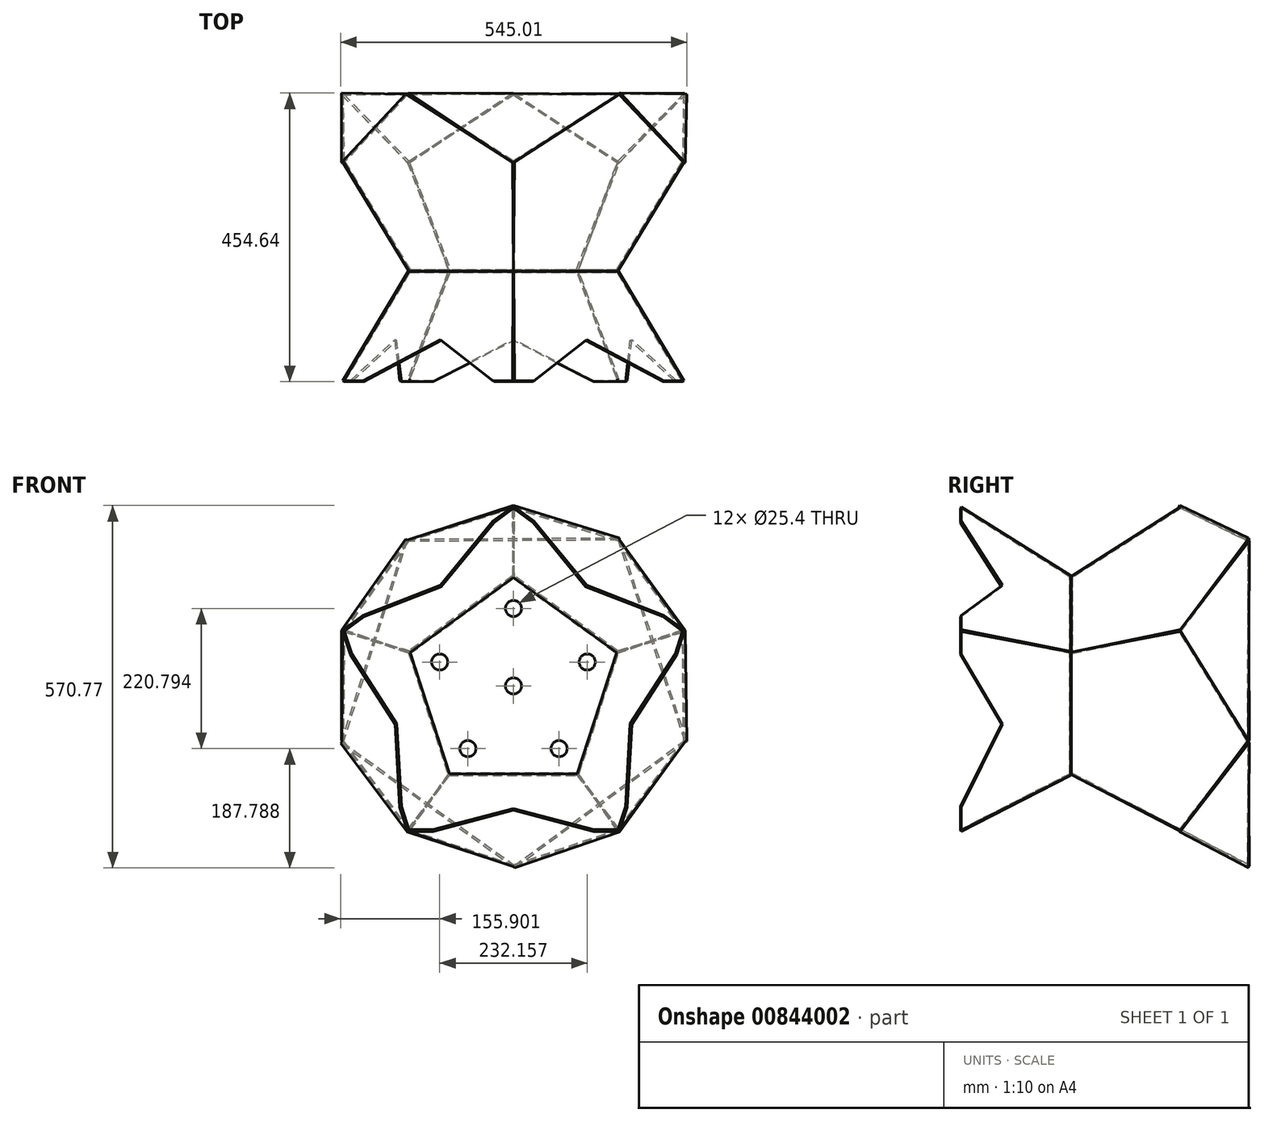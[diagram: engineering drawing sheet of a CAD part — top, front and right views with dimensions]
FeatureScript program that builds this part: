
annotation { "Feature Type Name" : "Feature", "Feature Type Description" : "" }
export const myFeature = defineFeature(function(context is Context, id is Id, definition is map)
    precondition{}
    {
        {
            var Q0;
            Q0=qCreatedBy(makeId("Front.planeOp"),FACE);
            var sketch = newSketch(context, id + "F0", { "sketchPlane" : qUnion([Q0])});
            skCircle(sketch, "E0.cCircle", {"center": v(0, 0) * mm, "radius": 139.84 * mm, "construction": true});
            skLineSegment(sketch, "E0.0", {"start": v(0, 172.85) * mm, "end": v(164.4, 53.41) * mm});
            skLineSegment(sketch, "E0.1", {"start": v(164.4, 53.41) * mm, "end": v(101.6, -139.84) * mm});
            skLineSegment(sketch, "E0.2", {"start": v(101.6, -139.84) * mm, "end": v(-101.6, -139.84) * mm});
            skLineSegment(sketch, "E0.3", {"start": v(-101.6, -139.84) * mm, "end": v(-164.4, 53.41) * mm});
            skLineSegment(sketch, "E0.4", {"start": v(-164.4, 53.41) * mm, "end": v(0, 172.85) * mm});
            skPoint(sketch, "E0.0.midPoint", {"position": v(82.2, 113.13) * mm});
            skCircle(sketch, "E1", {"center": v(0, 0) * mm, "radius": 122.05 * mm, "construction": true});
            skCircle(sketch, "E2", {"center": v(0, 122.05) * mm, "radius": 12.7 * mm});
            skCircle(sketch, "E3.1.0", {"center": v(-116.08, 37.72) * mm, "radius": 12.7 * mm});
            skCircle(sketch, "E3.2.0", {"center": v(-71.74, -98.74) * mm, "radius": 12.7 * mm});
            skCircle(sketch, "E4.1.3.0", {"center": v(71.74, -98.74) * mm, "radius": 12.7 * mm});
            skCircle(sketch, "E4.1.4.0", {"center": v(116.08, 37.72) * mm, "radius": 12.7 * mm});
            skCircle(sketch, "E5", {"center": v(0, 0) * mm, "radius": 12.7 * mm});
            skSolve(sketch);
        }
        {
            var Q0;
            Q0=makeQuery(id+"F0.imprint","IMPRINT",FACE,{"disambiguationData":[TD([[makeQuery(id+"F0.imprint","IMPRINT",EDGE,{"derivedFrom":sQuery(id+"F0.wireOp",EDGE,"E0.0")}),-1.0]])]});
            extrude(context, id + "F1", {"entities" : qUnion([Q0]), "endBound" : BoundingType.SYMMETRIC, "depth" : 3.17 * mm, "offsetDistance" : 25.4 * mm});
        }
        {
            var Q0;
            Q0=makeQuery(id+"F1.opExtrude","CAP_EDGE",EDGE,{"disambiguationData":[OSD([sQuery(id+"F0.wireOp",EDGE,"E0.1")])],"isStart":true});
            cPlane(context, id + "F2", {"entities" : qUnion([Q0]), "cplaneType" : CPlaneType.LINE_ANGLE, "offset" : 25.4 * mm, "angle" : 27.09 * degree, "oppositeDirection" : true, "width" : 152.4 * mm, "height" : 152.4 * mm});
        }
        {
            var Q0;
            Q0=qCreatedBy(id+"F2.planeOp",FACE);
            var sketch = newSketch(context, id + "F3", { "sketchPlane" : qUnion([Q0])});
            skArc(sketch, "E6.cCircle", {"start": v(258.35, 129.24) * mm, "mid": v(65.1, 0) * mm, "end": v(258.35, -129.24) * mm, "construction": true});
            skLineSegment(sketch, "E6.0", {"start": v(65.1, -101.6) * mm, "end": v(65.1, 101.6) * mm});
            skLineSegment(sketch, "E6.1", {"start": v(65.1, 101.6) * mm, "end": v(258.35, 164.4) * mm});
            skLineSegment(sketch, "E6.4", {"start": v(258.35, -164.4) * mm, "end": v(65.1, -101.6) * mm});
            skPoint(sketch, "E6.0.midPoint", {"position": v(65.1, 0) * mm});
            skLineSegment(sketch, "E7", {"start": v(258.35, 164.4) * mm, "end": v(258.35, 126.3) * mm});
            skLineSegment(sketch, "E8", {"start": v(258.35, 126.3) * mm, "end": v(185.44, 0) * mm});
            skLineSegment(sketch, "E9", {"start": v(258.35, -126.3) * mm, "end": v(185.44, 0) * mm});
            skLineSegment(sketch, "E10.trimOffspring", {"start": v(258.35, -126.3) * mm, "end": v(258.35, -164.4) * mm});
            skSolve(sketch);
        }
        {
            var Q0;
            Q0 = qSketchRegion(id + "F3", true);
            extrude(context, id + "F4", {"entities" : qUnion([Q0]), "depth" : 3.17 * mm, "offsetDistance" : 25.4 * mm});
        }
        {
            var Q0;
            Q0=makeQuery(id+"F4.opExtrude","SWEPT_BODY",BODY,{"disambiguationData":[OSD([sQuery(id+"F3.wireOp",EDGE,"E6.0"),sQuery(id+"F3.wireOp",EDGE,"E6.1"),sQuery(id+"F3.wireOp",EDGE,"E6.4"),sQuery(id+"F3.wireOp",EDGE,"E7"),sQuery(id+"F3.wireOp",EDGE,"E8"),sQuery(id+"F3.wireOp",EDGE,"E9"),sQuery(id+"F3.wireOp",EDGE,"E10.trimOffspring")])]});
            var Q1;
            Q1=sQuery(id+"F0.wireOp",EDGE,"E0.cCircle");
            circularPattern(context, id + "F5", {"entities" : qUnion([Q0]), "axis" : qUnion([Q1]), "angle" : 360 * degree, "instanceCount" : 5, "equalSpace" : true});
        }
        {
            var Q0;
            Q0=sQuery(id+"F0.wireOp",EDGE,"E0.0");
            cPlane(context, id + "F6", {"entities" : qUnion([Q0]), "cplaneType" : CPlaneType.LINE_ANGLE, "offset" : 25.4 * mm, "angle" : 62.5 * degree, "oppositeDirection" : true, "width" : 152.4 * mm, "height" : 152.4 * mm});
        }
        {
            var Q0;
            Q0=qCreatedBy(id+"F6.planeOp",FACE);
            var sketch = newSketch(context, id + "F7", { "sketchPlane" : qUnion([Q0])});
            skCircle(sketch, "E11.cCircle", {"center": v(65.01, -193.8) * mm, "radius": 139.84 * mm, "construction": true});
            skLineSegment(sketch, "E11.0", {"start": v(120, -357.67) * mm, "end": v(-73.85, -296.72) * mm});
            skLineSegment(sketch, "E11.1", {"start": v(-73.85, -296.72) * mm, "end": v(-75.79, -93.53) * mm});
            skLineSegment(sketch, "E11.2", {"start": v(-75.79, -93.53) * mm, "end": v(116.86, -28.9) * mm});
            skLineSegment(sketch, "E11.3", {"start": v(116.86, -28.9) * mm, "end": v(237.86, -192.15) * mm});
            skLineSegment(sketch, "E11.4", {"start": v(237.86, -192.15) * mm, "end": v(120, -357.67) * mm});
            skPoint(sketch, "E11.0.midPoint", {"position": v(23.07, -327.2) * mm});
            skSolve(sketch);
        }
        {
            var Q0;
            Q0 = qSketchRegion(id + "F7", true);
            extrude(context, id + "F8", {"entities" : qUnion([Q0]), "depth" : 3.17 * mm, "offsetDistance" : 25.4 * mm});
        }
        {
            var Q0;
            Q0=makeQuery(id+"F8.opExtrude","SWEPT_BODY",BODY,{"disambiguationData":[OSD([sQuery(id+"F7.wireOp",EDGE,"E11.0"),sQuery(id+"F7.wireOp",EDGE,"E11.1"),sQuery(id+"F7.wireOp",EDGE,"E11.2"),sQuery(id+"F7.wireOp",EDGE,"E11.3"),sQuery(id+"F7.wireOp",EDGE,"E11.4")])]});
            var Q1;
            Q1=sQuery(id+"F0.wireOp",EDGE,"E0.cCircle");
            circularPattern(context, id + "F9", {"entities" : qUnion([Q0]), "axis" : qUnion([Q1]), "angle" : 360 * degree, "instanceCount" : 5, "equalSpace" : true});
        }
        {
            var Q0;
            Q0=makeQuery(id+"F9.opPattern","COPY",VERTEX,{"derivedFrom":makeQuery(id+"F8.opExtrude","CAP_VERTEX",VERTEX,{"disambiguationData":[OSD([sQuery(id+"F7.wireOp",EDGE,"E11.0"),sQuery(id+"F7.wireOp",EDGE,"E11.4")])],"isStart":false}),"instanceName":"2"});
            var Q1;
            Q1=makeQuery(id+"F9.opPattern","COPY",VERTEX,{"derivedFrom":makeQuery(id+"F8.opExtrude","CAP_VERTEX",VERTEX,{"disambiguationData":[OSD([sQuery(id+"F7.wireOp",EDGE,"E11.0"),sQuery(id+"F7.wireOp",EDGE,"E11.4")])],"isStart":true}),"instanceName":"1"});
            var Q2;
            Q2=makeQuery(id+"F9.opPattern","COPY",VERTEX,{"derivedFrom":makeQuery(id+"F8.opExtrude","CAP_VERTEX",VERTEX,{"disambiguationData":[OSD([sQuery(id+"F7.wireOp",EDGE,"E11.0"),sQuery(id+"F7.wireOp",EDGE,"E11.1")])],"isStart":false}),"instanceName":"1"});
            cPlane(context, id + "F10", {"entities" : qUnion([Q0, Q1, Q2]), "cplaneType" : CPlaneType.THREE_POINT, "offset" : 25.4 * mm, "width" : 152.4 * mm, "height" : 152.4 * mm});
        }
        {
            var Q0;
            Q0=qCreatedBy(id+"F10.planeOp",FACE);
            var sketch = newSketch(context, id + "F11", { "sketchPlane" : qUnion([Q0])});
            skArc(sketch, "E12.cCircle", {"start": v(-151.4, -128.78) * mm, "mid": v(-63.36, 1.48) * mm, "end": v(-150.12, 132.6) * mm, "construction": true});
            skLineSegment(sketch, "E12.0", {"start": v(-29.98, 1.32) * mm, "end": v(-151.57, -164.33) * mm});
            skLineSegment(sketch, "E12.4", {"start": v(-149.95, 168.15) * mm, "end": v(-29.98, 1.32) * mm});
            skPoint(sketch, "E12.0.midPoint", {"position": v(-90.78, -81.5) * mm});
            skLineSegment(sketch, "E13", {"start": v(-149.95, 168.15) * mm, "end": v(-151.57, -164.33) * mm});
            skSolve(sketch);
        }
        {
            var Q0;
            Q0=makeQuery(id+"F11.imprint","IMPRINT",FACE,{"disambiguationData":[TD([[makeQuery(id+"F11.imprint","IMPRINT",EDGE,{"derivedFrom":sQuery(id+"F11.wireOp",EDGE,"E12.0")}),-1.0]])]});
            extrude(context, id + "F12", {"entities" : qUnion([Q0]), "depth" : 3.17 * mm, "offsetDistance" : 25.4 * mm});
        }
        {
            var Q0;
            Q0=makeQuery(id+"F12.opExtrude","SWEPT_BODY",BODY,{"disambiguationData":[OSD([sQuery(id+"F11.wireOp",EDGE,"E12.0"),sQuery(id+"F11.wireOp",EDGE,"E12.4"),sQuery(id+"F11.wireOp",EDGE,"E13")])]});
            var Q1;
            Q1=sQuery(id+"F0.wireOp",EDGE,"E0.cCircle");
            circularPattern(context, id + "F13", {"entities" : qUnion([Q0]), "axis" : qUnion([Q1]), "angle" : 360 * degree, "instanceCount" : 5, "equalSpace" : true});
        }
        {
            var Q0;
            Q0=makeQuery(id+"F1.opExtrude","SWEPT_BODY",BODY,{"disambiguationData":[OSD([sQuery(id+"F0.wireOp",EDGE,"E0.0"),sQuery(id+"F0.wireOp",EDGE,"E0.1"),sQuery(id+"F0.wireOp",EDGE,"E0.2"),sQuery(id+"F0.wireOp",EDGE,"E0.3"),sQuery(id+"F0.wireOp",EDGE,"E0.4"),sQuery(id+"F0.wireOp",EDGE,"E2"),sQuery(id+"F0.wireOp",EDGE,"E3.1.0"),sQuery(id+"F0.wireOp",EDGE,"E3.2.0"),sQuery(id+"F0.wireOp",EDGE,"E4.1.3.0"),sQuery(id+"F0.wireOp",EDGE,"E4.1.4.0"),sQuery(id+"F0.wireOp",EDGE,"E5")])]});
            transform(context, id + "F14", {"entities" : qUnion([Q0]), "transformType" : TransformType.TRANSLATION_3D, "dx" : 0 * mm, "dy" : 0 * mm, "dz" : 0 * mm, "makeCopy" : true});
        }
    });
